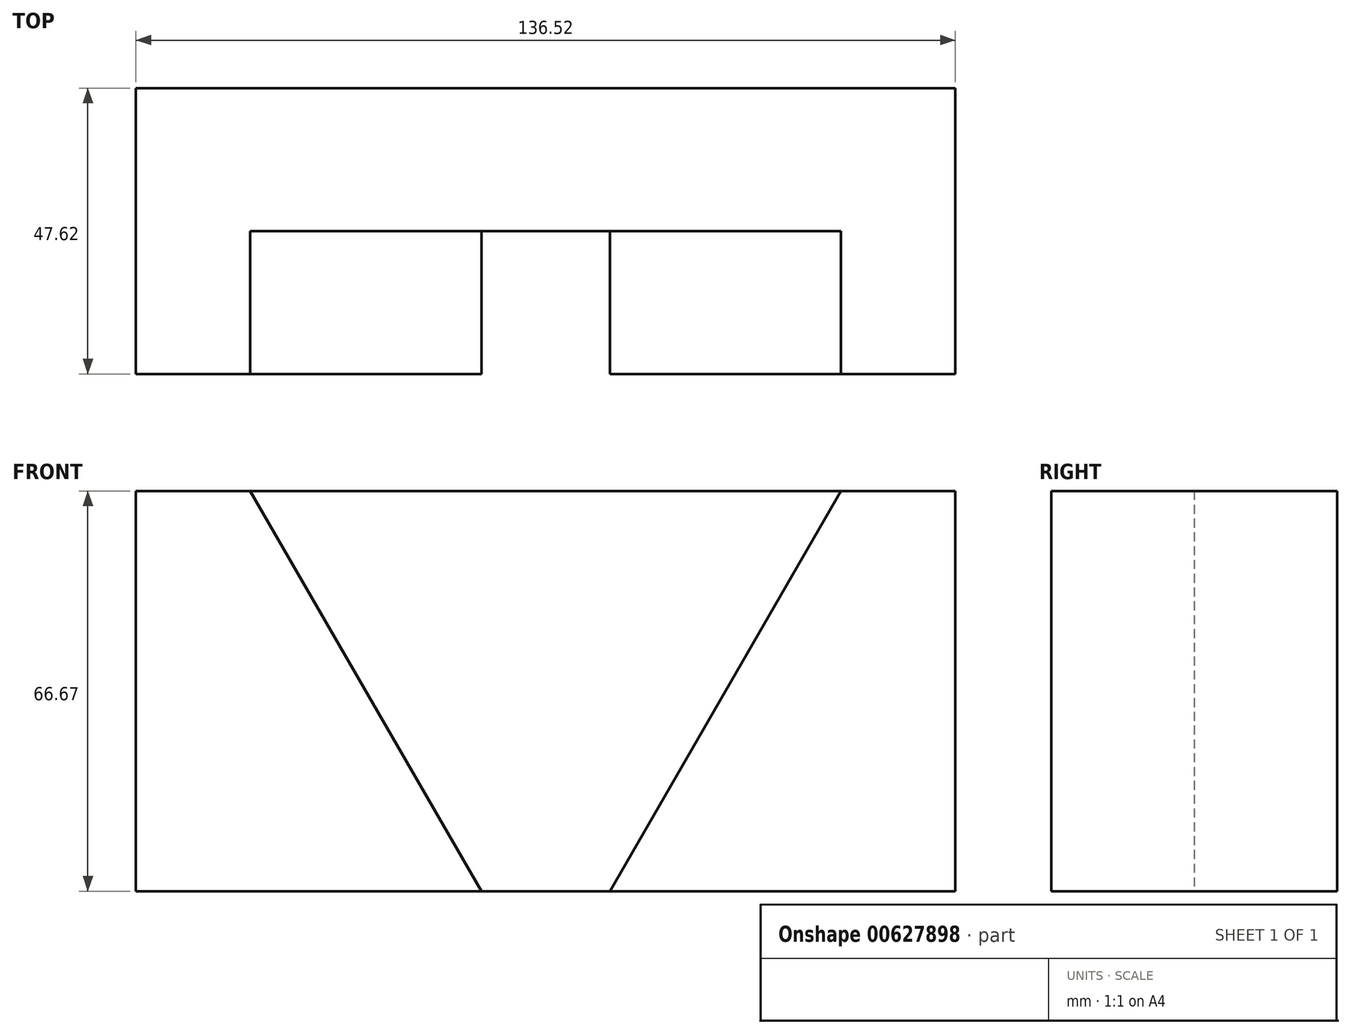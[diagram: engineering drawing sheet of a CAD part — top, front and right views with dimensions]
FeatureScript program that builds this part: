
annotation { "Feature Type Name" : "Feature", "Feature Type Description" : "" }
export const myFeature = defineFeature(function(context is Context, id is Id, definition is map)
    precondition{}
    {
        {
            var Q0;
            Q0=qCreatedBy(makeId("Front.planeOp"),FACE);
            var sketch = newSketch(context, id + "F0", { "sketchPlane" : qUnion([Q0])});
            skLineSegment(sketch, "E0.bottom", {"start": v(-58.18, 19.84) * mm, "end": v(78.34, 19.84) * mm});
            skLineSegment(sketch, "E0.top", {"start": v(-58.18, -46.83) * mm, "end": v(78.34, -46.83) * mm});
            skLineSegment(sketch, "E0.left", {"start": v(-58.18, 19.84) * mm, "end": v(-58.18, -46.83) * mm});
            skLineSegment(sketch, "E0.right", {"start": v(78.34, 19.84) * mm, "end": v(78.34, -46.83) * mm});
            skSolve(sketch);
        }
        {
            var Q0;
            Q0=makeQuery(id+"F0.imprint","IMPRINT",FACE,{"disambiguationData":[TD([[makeQuery(id+"F0.imprint","IMPRINT",EDGE,{"derivedFrom":sQuery(id+"F0.wireOp",EDGE,"E0.bottom")}),-1.0]])]});
            extrude(context, id + "F1", {"entities" : qUnion([Q0]), "depth" : 47.62 * mm, "offsetDistance" : 25.4 * mm});
        }
        {
            var Q0;
            Q0=makeQuery(id+"F1.opExtrude","CAP_FACE",FACE,{"disambiguationData":[OSD([sQuery(id+"F0.wireOp",EDGE,"E0.bottom"),sQuery(id+"F0.wireOp",EDGE,"E0.top"),sQuery(id+"F0.wireOp",EDGE,"E0.left"),sQuery(id+"F0.wireOp",EDGE,"E0.right")])],"isStart":false});
            var sketch = newSketch(context, id + "F2", { "sketchPlane" : qUnion([Q0])});
            skLineSegment(sketch, "E1", {"start": v(-39.13, 19.84) * mm, "end": v(-0.64, -46.83) * mm});
            skLineSegment(sketch, "E2", {"start": v(59.3, 19.84) * mm, "end": v(20.8, -46.83) * mm});
            skSolve(sketch);
        }
        {
            var Q0;
            {var subQ0=sQuery(id+"F2.wireOp",EDGE,"E1");Q0=makeQuery(id+"F2.imprint","IMPRINT",FACE,{"disambiguationData":[TD([[makeQuery(id+"F2.imprint","IMPRINT",EDGE,{"derivedFrom":subQ0}),1.0]])]});}
            extrude(context, id + "F3", {"entities" : qUnion([Q0]), "operationType" : NewBodyOperationType.REMOVE, "oppositeDirection" : true, "depth" : 23.8 * mm, "offsetDistance" : 25.4 * mm});
        }
    });
